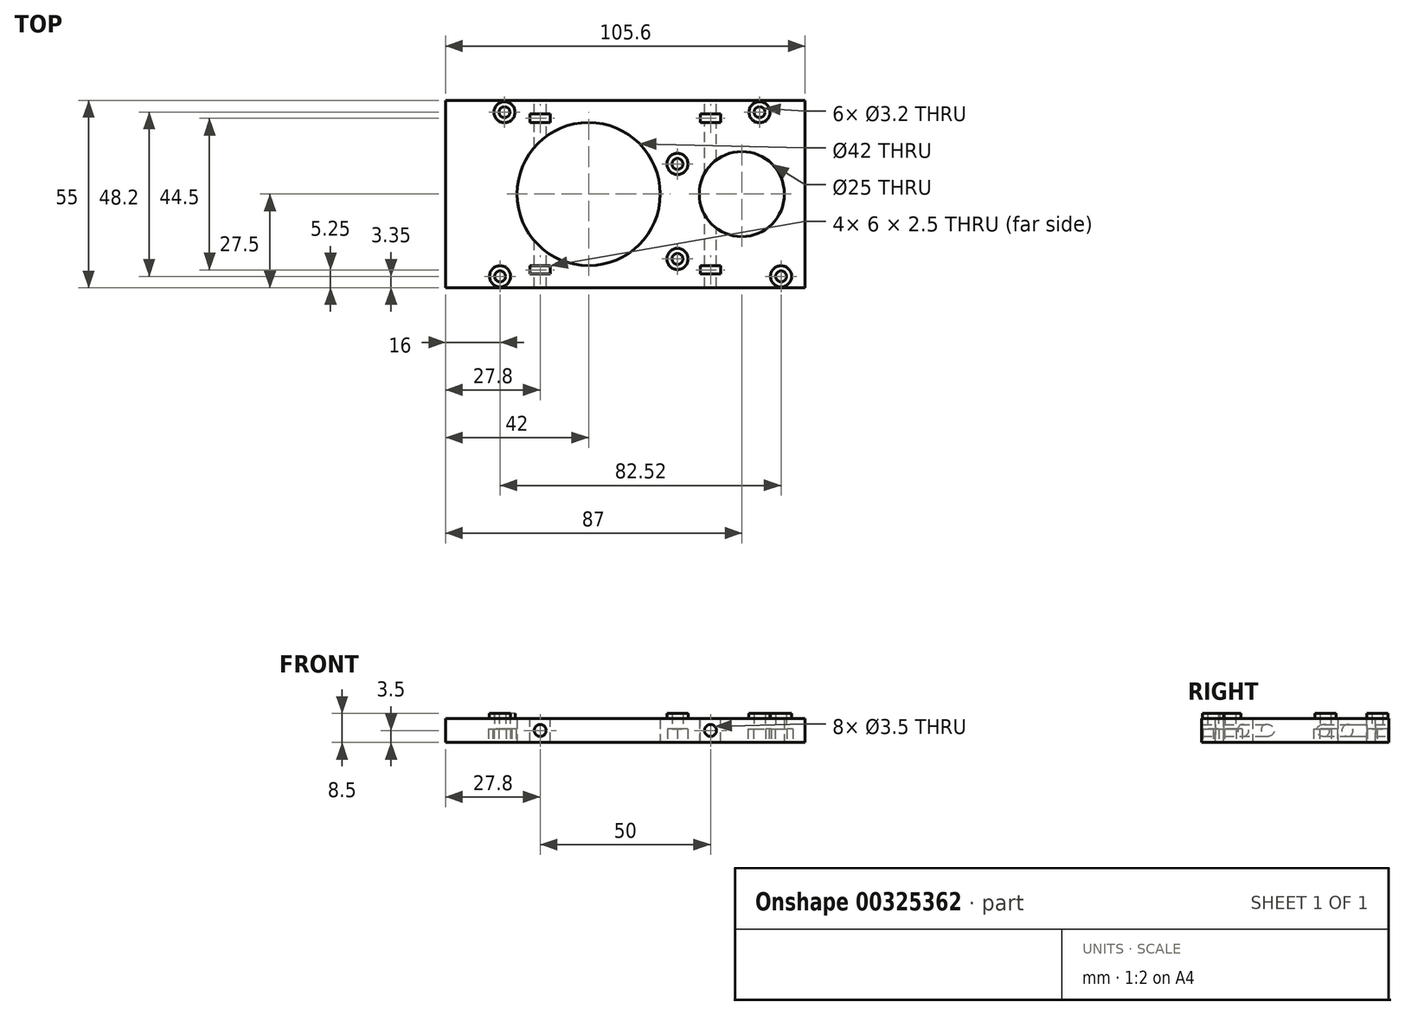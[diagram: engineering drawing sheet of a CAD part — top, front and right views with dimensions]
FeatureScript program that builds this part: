
annotation { "Feature Type Name" : "Feature", "Feature Type Description" : "" }
export const myFeature = defineFeature(function(context is Context, id is Id, definition is map)
    precondition{}
    {
        {
            var Q0;
            Q0=qCreatedBy(makeId("Top.planeOp"),FACE);
            var sketch = newSketch(context, id + "F0", { "sketchPlane" : qUnion([Q0])});
            skLineSegment(sketch, "E0.bottom", {"start": v(0, 0) * mm, "end": v(101.6, 0) * mm, "construction": true});
            skLineSegment(sketch, "E0.top", {"start": v(0, 53.3) * mm, "end": v(101.6, 53.3) * mm, "construction": true});
            skLineSegment(sketch, "E0.left", {"start": v(0, 0) * mm, "end": v(0, 53.3) * mm, "construction": true});
            skLineSegment(sketch, "E0.right", {"start": v(101.6, 0) * mm, "end": v(101.6, 53.3) * mm, "construction": true});
            skCircle(sketch, "E1", {"center": v(15.3, 50.7) * mm, "radius": 1.6 * mm});
            skCircle(sketch, "E2", {"center": v(90.2, 50.7) * mm, "radius": 1.6 * mm});
            skCircle(sketch, "E3", {"center": v(66.1, 35.5) * mm, "radius": 1.6 * mm});
            skCircle(sketch, "E4", {"center": v(66.1, 7.6) * mm, "radius": 1.6 * mm});
            skCircle(sketch, "E5", {"center": v(96.52, 2.5) * mm, "radius": 1.6 * mm});
            skCircle(sketch, "E6", {"center": v(14, 2.5) * mm, "radius": 1.6 * mm});
            skLineSegment(sketch, "E7.bottom", {"start": v(-2, 54.15) * mm, "end": v(103.6, 54.15) * mm});
            skLineSegment(sketch, "E7.top", {"start": v(-2, -0.85) * mm, "end": v(103.6, -0.85) * mm});
            skLineSegment(sketch, "E7.left", {"start": v(-2, 54.15) * mm, "end": v(-2, -0.85) * mm});
            skLineSegment(sketch, "E7.right", {"start": v(103.6, 54.15) * mm, "end": v(103.6, -0.85) * mm});
            skLineSegment(sketch, "E8", {"start": v(0, 0) * mm, "end": v(0, -0.85) * mm, "construction": true});
            skLineSegment(sketch, "E9", {"start": v(0, 53.3) * mm, "end": v(0, 54.15) * mm, "construction": true});
            skLineSegment(sketch, "E10", {"start": v(0, 0) * mm, "end": v(-2, 0) * mm, "construction": true});
            skLineSegment(sketch, "E11", {"start": v(101.6, 0) * mm, "end": v(103.6, 0) * mm, "construction": true});
            skCircle(sketch, "E12", {"center": v(40, 26.65) * mm, "radius": 21 * mm});
            skPoint(sketch, "E12.centerSnap0", {"position": v(0, 26.65) * mm});
            skCircle(sketch, "E13", {"center": v(85, 26.65) * mm, "radius": 12.5 * mm});
            skPoint(sketch, "E13.centerSnap0", {"position": v(101.6, 26.65) * mm});
            skSolve(sketch);
        }
        {
            var Q0;
            Q0 = qSketchRegion(id + "F0", true);
            extrude(context, id + "F1", {"entities" : qUnion([Q0]), "depth" : 7 * mm});
        }
        {
            var Q0;
            Q0=makeQuery(id+"F1.opExtrude","CAP_FACE",FACE,{"disambiguationData":[OSD([sQuery(id+"F0.wireOp",EDGE,"E1"),sQuery(id+"F0.wireOp",EDGE,"E2"),sQuery(id+"F0.wireOp",EDGE,"E3"),sQuery(id+"F0.wireOp",EDGE,"E4"),sQuery(id+"F0.wireOp",EDGE,"E5"),sQuery(id+"F0.wireOp",EDGE,"E6"),sQuery(id+"F0.wireOp",EDGE,"E7.bottom"),sQuery(id+"F0.wireOp",EDGE,"E7.top"),sQuery(id+"F0.wireOp",EDGE,"E7.left"),sQuery(id+"F0.wireOp",EDGE,"E7.right")])],"isStart":false});
            var sketch = newSketch(context, id + "F2", { "sketchPlane" : qUnion([Q0])});
            skCircle(sketch, "E14", {"center": v(15.3, 50.7) * mm, "radius": 3.1 * mm});
            skCircle(sketch, "E15", {"center": v(90.2, 50.7) * mm, "radius": 3.1 * mm});
            skCircle(sketch, "E16", {"center": v(66.1, 35.5) * mm, "radius": 3.1 * mm});
            skCircle(sketch, "E17", {"center": v(66.1, 7.6) * mm, "radius": 3.1 * mm});
            skCircle(sketch, "E18", {"center": v(96.52, 2.5) * mm, "radius": 3.1 * mm});
            skCircle(sketch, "E19", {"center": v(14, 2.5) * mm, "radius": 3.1 * mm});
            skCircle(sketch, "E20.0", {"center": v(15.3, 50.7) * mm, "radius": 1.6 * mm});
            skCircle(sketch, "E21.0", {"center": v(66.1, 35.5) * mm, "radius": 1.6 * mm});
            skCircle(sketch, "E22.1", {"center": v(14, 2.5) * mm, "radius": 1.6 * mm});
            skCircle(sketch, "E23.2", {"center": v(66.1, 7.6) * mm, "radius": 1.6 * mm});
            skCircle(sketch, "E24.0", {"center": v(90.2, 50.7) * mm, "radius": 1.6 * mm});
            skCircle(sketch, "E25.0", {"center": v(96.52, 2.5) * mm, "radius": 1.6 * mm});
            skSolve(sketch);
        }
        {
            var Q0;
            Q0 = qSketchRegion(id + "F2", true);
            extrude(context, id + "F3", {"entities" : qUnion([Q0]), "operationType" : NewBodyOperationType.ADD, "depth" : 1.5 * mm});
        }
        {
            var Q0;
            Q0=makeQuery(id+"F1.opExtrude","CAP_FACE",FACE,{"disambiguationData":[OSD([sQuery(id+"F0.wireOp",EDGE,"E1"),sQuery(id+"F0.wireOp",EDGE,"E2"),sQuery(id+"F0.wireOp",EDGE,"E3"),sQuery(id+"F0.wireOp",EDGE,"E4"),sQuery(id+"F0.wireOp",EDGE,"E5"),sQuery(id+"F0.wireOp",EDGE,"E6"),sQuery(id+"F0.wireOp",EDGE,"E7.bottom"),sQuery(id+"F0.wireOp",EDGE,"E7.top"),sQuery(id+"F0.wireOp",EDGE,"E7.left"),sQuery(id+"F0.wireOp",EDGE,"E7.right")])],"isStart":false});
            var sketch = newSketch(context, id + "F4", { "sketchPlane" : qUnion([Q0])});
            skLineSegment(sketch, "E26.bottom", {"start": v(78.8, 50.15) * mm, "end": v(72.8, 50.15) * mm});
            skLineSegment(sketch, "E26.top", {"start": v(78.8, 47.65) * mm, "end": v(72.8, 47.65) * mm});
            skLineSegment(sketch, "E26.left", {"start": v(78.8, 50.15) * mm, "end": v(78.8, 47.65) * mm});
            skLineSegment(sketch, "E26.right", {"start": v(72.8, 50.15) * mm, "end": v(72.8, 47.65) * mm});
            skLineSegment(sketch, "E27.bottom", {"start": v(78.8, 5.65) * mm, "end": v(72.8, 5.65) * mm});
            skLineSegment(sketch, "E27.top", {"start": v(78.8, 3.15) * mm, "end": v(72.8, 3.15) * mm});
            skLineSegment(sketch, "E27.left", {"start": v(78.8, 5.65) * mm, "end": v(78.8, 3.15) * mm});
            skLineSegment(sketch, "E27.right", {"start": v(72.8, 5.65) * mm, "end": v(72.8, 3.15) * mm});
            skLineSegment(sketch, "E28.bottom", {"start": v(28.8, 50.15) * mm, "end": v(22.8, 50.15) * mm});
            skLineSegment(sketch, "E28.top", {"start": v(28.8, 47.65) * mm, "end": v(22.8, 47.65) * mm});
            skLineSegment(sketch, "E28.left", {"start": v(28.8, 50.15) * mm, "end": v(28.8, 47.65) * mm});
            skLineSegment(sketch, "E28.right", {"start": v(22.8, 50.15) * mm, "end": v(22.8, 47.65) * mm});
            skLineSegment(sketch, "E29.bottom", {"start": v(28.8, 5.65) * mm, "end": v(22.8, 5.65) * mm});
            skLineSegment(sketch, "E29.top", {"start": v(28.8, 3.15) * mm, "end": v(22.8, 3.15) * mm});
            skLineSegment(sketch, "E29.left", {"start": v(28.8, 5.65) * mm, "end": v(28.8, 3.15) * mm});
            skLineSegment(sketch, "E29.right", {"start": v(22.8, 5.65) * mm, "end": v(22.8, 3.15) * mm});
            skLineSegment(sketch, "E30", {"start": v(75.8, 54.15) * mm, "end": v(75.8, -0.85) * mm, "construction": true});
            skPoint(sketch, "E30.startSnap0", {"position": v(75.8, 50.15) * mm});
            skPoint(sketch, "E30.endSnap0", {"position": v(75.8, 3.15) * mm});
            skLineSegment(sketch, "E31", {"start": v(25.8, 54.15) * mm, "end": v(25.8, 0) * mm, "construction": true});
            skPoint(sketch, "E31.startSnap0", {"position": v(25.8, 47.65) * mm});
            skPoint(sketch, "E31.endSnap0", {"position": v(25.8, 3.15) * mm});
            skLineSegment(sketch, "E32", {"start": v(72.8, 50.15) * mm, "end": v(28.8, 50.15) * mm, "construction": true});
            skLineSegment(sketch, "E33", {"start": v(72.8, 3.15) * mm, "end": v(28.8, 3.15) * mm, "construction": true});
            skLineSegment(sketch, "E34", {"start": v(78.8, 50.15) * mm, "end": v(78.8, 54.15) * mm, "construction": true});
            skLineSegment(sketch, "E35", {"start": v(78.8, 3.15) * mm, "end": v(78.8, -0.85) * mm, "construction": true});
            skLineSegment(sketch, "E36", {"start": v(25.8, 27.08) * mm, "end": v(-2, 27.08) * mm, "construction": true});
            skLineSegment(sketch, "E37", {"start": v(75.8, 26.65) * mm, "end": v(103.6, 26.65) * mm, "construction": true});
            skSolve(sketch);
        }
        {
            var Q0;
            Q0 = qSketchRegion(id + "F4", true);
            extrude(context, id + "F5", {"entities" : qUnion([Q0]), "operationType" : NewBodyOperationType.REMOVE, "endBound" : BoundingType.THROUGH_ALL, "oppositeDirection" : true, "depth" : 25 * mm});
        }
        {
            var Q0;
            Q0=makeQuery(id+"F1.opExtrude","CAP_FACE",FACE,{"disambiguationData":[OSD([sQuery(id+"F0.wireOp",EDGE,"E1"),sQuery(id+"F0.wireOp",EDGE,"E2"),sQuery(id+"F0.wireOp",EDGE,"E3"),sQuery(id+"F0.wireOp",EDGE,"E4"),sQuery(id+"F0.wireOp",EDGE,"E5"),sQuery(id+"F0.wireOp",EDGE,"E6"),sQuery(id+"F0.wireOp",EDGE,"E7.bottom"),sQuery(id+"F0.wireOp",EDGE,"E7.top"),sQuery(id+"F0.wireOp",EDGE,"E7.left"),sQuery(id+"F0.wireOp",EDGE,"E7.right")])],"isStart":true});
            var sketch = newSketch(context, id + "F6", { "sketchPlane" : qUnion([Q0])});
            skCircle(sketch, "E38.cCircle", {"center": v(14, -2.5) * mm, "radius": 3 * mm, "construction": true});
            skLineSegment(sketch, "E38.0", {"start": v(15.73, -5.5) * mm, "end": v(12.27, -5.5) * mm});
            skLineSegment(sketch, "E38.1", {"start": v(12.27, -5.5) * mm, "end": v(10.54, -2.5) * mm});
            skLineSegment(sketch, "E38.2", {"start": v(10.54, -2.5) * mm, "end": v(12.27, 0.5) * mm});
            skLineSegment(sketch, "E38.3", {"start": v(12.27, 0.5) * mm, "end": v(15.73, 0.5) * mm});
            skLineSegment(sketch, "E38.4", {"start": v(15.73, 0.5) * mm, "end": v(17.46, -2.5) * mm});
            skLineSegment(sketch, "E38.5", {"start": v(17.46, -2.5) * mm, "end": v(15.73, -5.5) * mm});
            skCircle(sketch, "E39.cCircle", {"center": v(96.52, -2.5) * mm, "radius": 3 * mm, "construction": true});
            skLineSegment(sketch, "E39.0", {"start": v(94.79, 0.5) * mm, "end": v(98.25, 0.5) * mm});
            skLineSegment(sketch, "E39.1", {"start": v(98.25, 0.5) * mm, "end": v(99.98, -2.5) * mm});
            skLineSegment(sketch, "E39.2", {"start": v(99.98, -2.5) * mm, "end": v(98.25, -5.5) * mm});
            skLineSegment(sketch, "E39.3", {"start": v(98.25, -5.5) * mm, "end": v(94.79, -5.5) * mm});
            skLineSegment(sketch, "E39.4", {"start": v(94.79, -5.5) * mm, "end": v(93.06, -2.5) * mm});
            skLineSegment(sketch, "E39.5", {"start": v(93.06, -2.5) * mm, "end": v(94.79, 0.5) * mm});
            skPoint(sketch, "E39.0.midPoint", {"position": v(96.52, 0.5) * mm});
            skCircle(sketch, "E40.cCircle", {"center": v(66.1, -7.6) * mm, "radius": 3 * mm, "construction": true});
            skLineSegment(sketch, "E40.0", {"start": v(63.1, -9.33) * mm, "end": v(63.1, -5.87) * mm});
            skLineSegment(sketch, "E40.1", {"start": v(63.1, -5.87) * mm, "end": v(66.1, -4.14) * mm});
            skLineSegment(sketch, "E40.2", {"start": v(66.1, -4.14) * mm, "end": v(69.1, -5.87) * mm});
            skLineSegment(sketch, "E40.3", {"start": v(69.1, -5.87) * mm, "end": v(69.1, -9.33) * mm});
            skLineSegment(sketch, "E40.4", {"start": v(69.1, -9.33) * mm, "end": v(66.1, -11.06) * mm});
            skLineSegment(sketch, "E40.5", {"start": v(66.1, -11.06) * mm, "end": v(63.1, -9.33) * mm});
            skPoint(sketch, "E40.0.midPoint", {"position": v(63.1, -7.6) * mm});
            skCircle(sketch, "E41.cCircle", {"center": v(66.1, -35.5) * mm, "radius": 3 * mm, "construction": true});
            skLineSegment(sketch, "E41.0", {"start": v(63.1, -37.23) * mm, "end": v(63.1, -33.77) * mm});
            skLineSegment(sketch, "E41.1", {"start": v(63.1, -33.77) * mm, "end": v(66.1, -32.04) * mm});
            skLineSegment(sketch, "E41.2", {"start": v(66.1, -32.04) * mm, "end": v(69.1, -33.77) * mm});
            skLineSegment(sketch, "E41.3", {"start": v(69.1, -33.77) * mm, "end": v(69.1, -37.23) * mm});
            skLineSegment(sketch, "E41.4", {"start": v(69.1, -37.23) * mm, "end": v(66.1, -38.96) * mm});
            skLineSegment(sketch, "E41.5", {"start": v(66.1, -38.96) * mm, "end": v(63.1, -37.23) * mm});
            skPoint(sketch, "E41.0.midPoint", {"position": v(63.1, -35.5) * mm});
            skCircle(sketch, "E42.cCircle", {"center": v(90.2, -50.7) * mm, "radius": 3 * mm, "construction": true});
            skLineSegment(sketch, "E42.0", {"start": v(88.47, -47.7) * mm, "end": v(91.93, -47.7) * mm});
            skLineSegment(sketch, "E42.1", {"start": v(91.93, -47.7) * mm, "end": v(93.66, -50.7) * mm});
            skLineSegment(sketch, "E42.2", {"start": v(93.66, -50.7) * mm, "end": v(91.93, -53.7) * mm});
            skLineSegment(sketch, "E42.3", {"start": v(91.93, -53.7) * mm, "end": v(88.47, -53.7) * mm});
            skLineSegment(sketch, "E42.4", {"start": v(88.47, -53.7) * mm, "end": v(86.74, -50.7) * mm});
            skLineSegment(sketch, "E42.5", {"start": v(86.74, -50.7) * mm, "end": v(88.47, -47.7) * mm});
            skPoint(sketch, "E42.0.midPoint", {"position": v(90.2, -47.7) * mm});
            skCircle(sketch, "E43.cCircle", {"center": v(15.3, -50.7) * mm, "radius": 3 * mm, "construction": true});
            skLineSegment(sketch, "E43.0", {"start": v(11.84, -50.7) * mm, "end": v(13.57, -47.7) * mm});
            skLineSegment(sketch, "E43.1", {"start": v(13.57, -47.7) * mm, "end": v(17.03, -47.7) * mm});
            skLineSegment(sketch, "E43.2", {"start": v(17.03, -47.7) * mm, "end": v(18.76, -50.7) * mm});
            skLineSegment(sketch, "E43.3", {"start": v(18.76, -50.7) * mm, "end": v(17.03, -53.7) * mm});
            skLineSegment(sketch, "E43.4", {"start": v(17.03, -53.7) * mm, "end": v(13.57, -53.7) * mm});
            skLineSegment(sketch, "E43.5", {"start": v(13.57, -53.7) * mm, "end": v(11.84, -50.7) * mm});
            skPoint(sketch, "E43.0.midPoint", {"position": v(12.7, -49.2) * mm});
            skSolve(sketch);
        }
        {
            var Q0;
            Q0 = qSketchRegion(id + "F6", true);
            extrude(context, id + "F7", {"entities" : qUnion([Q0]), "operationType" : NewBodyOperationType.REMOVE, "oppositeDirection" : true, "depth" : 4 * mm});
        }
        {
            var Q0;
            Q0=makeQuery(id+"F1.opExtrude","SWEPT_FACE",FACE,{"disambiguationData":[OSD([sQuery(id+"F0.wireOp",EDGE,"E7.bottom")])]});
            var sketch = newSketch(context, id + "F8", { "sketchPlane" : qUnion([Q0])});
            skPoint(sketch, "E44.0", {"position": v(-75.8, 7) * mm});
            skPoint(sketch, "E45.0", {"position": v(-25.8, 7) * mm});
            skLineSegment(sketch, "E46", {"start": v(-75.8, 7) * mm, "end": v(-75.8, 0) * mm, "construction": true});
            skLineSegment(sketch, "E47", {"start": v(-25.8, 7) * mm, "end": v(-25.8, 0) * mm, "construction": true});
            skLineSegment(sketch, "E48", {"start": v(-75.8, 3.5) * mm, "end": v(-25.8, 3.5) * mm, "construction": true});
            skCircle(sketch, "E49", {"center": v(-75.8, 3.5) * mm, "radius": 1.75 * mm});
            skCircle(sketch, "E50", {"center": v(-25.8, 3.5) * mm, "radius": 1.75 * mm});
            skSolve(sketch);
        }
        {
            var Q0;
            Q0 = qSketchRegion(id + "F8", true);
            extrude(context, id + "F9", {"entities" : qUnion([Q0]), "operationType" : NewBodyOperationType.REMOVE, "endBound" : BoundingType.THROUGH_ALL, "oppositeDirection" : true, "depth" : 25 * mm});
        }
    });
